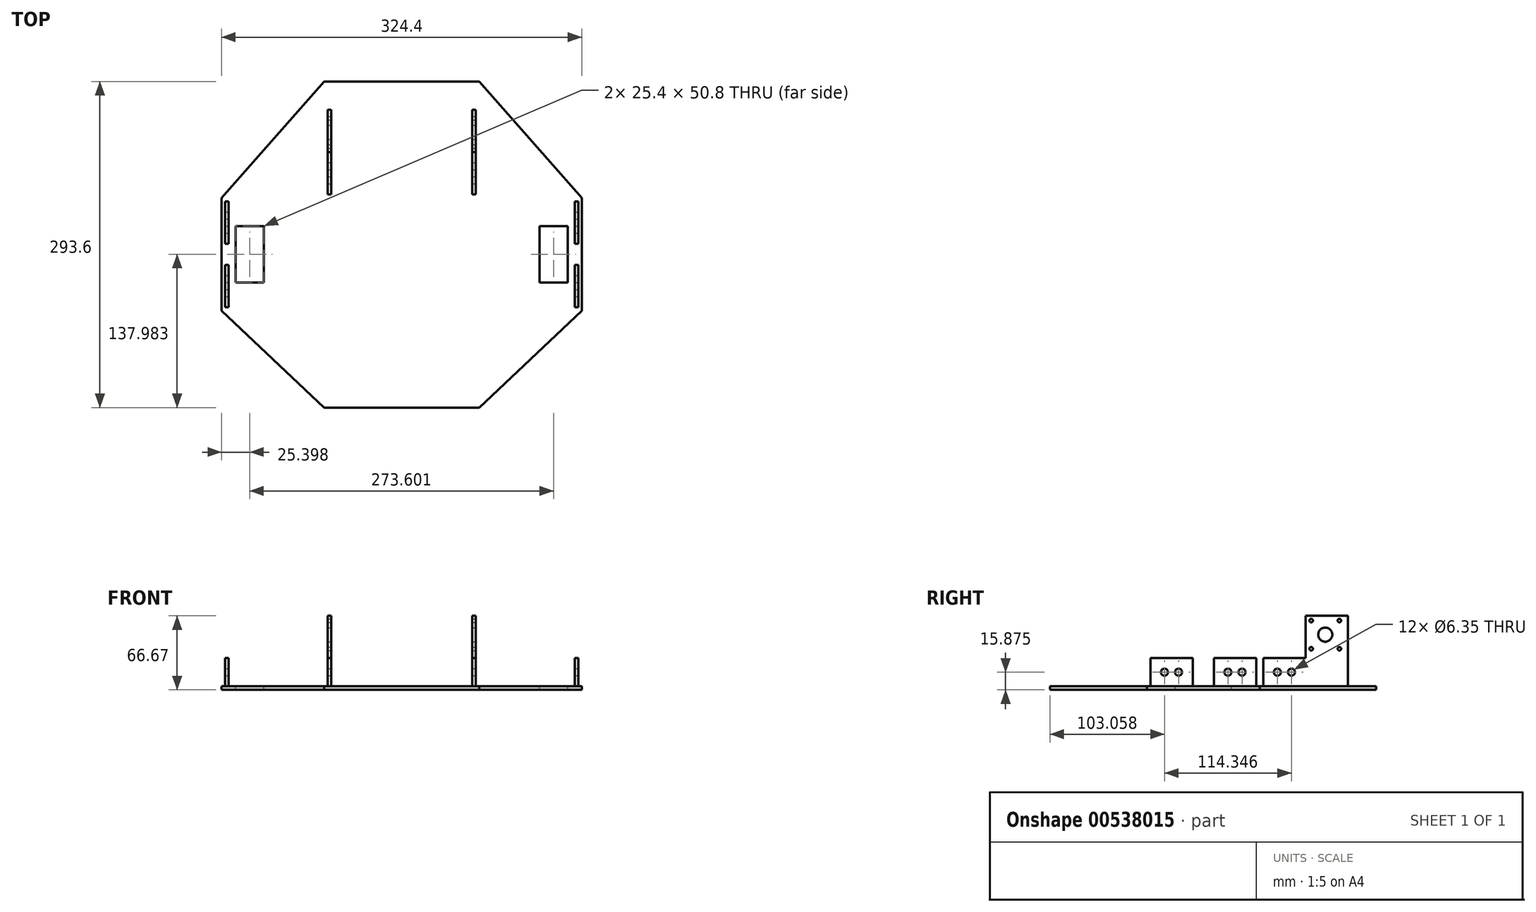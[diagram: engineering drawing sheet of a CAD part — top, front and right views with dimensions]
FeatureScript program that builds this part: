
annotation { "Feature Type Name" : "Feature", "Feature Type Description" : "" }
export const myFeature = defineFeature(function(context is Context, id is Id, definition is map)
    precondition{}
    {
        {
            var Q0;
            Q0=qCreatedBy(makeId("Top.planeOp"),FACE);
            var sketch = newSketch(context, id + "F0", { "sketchPlane" : qUnion([Q0])});
            skLineSegment(sketch, "E0", {"start": v(-252.95, -27.56) * mm, "end": v(-160.6, -114.74) * mm});
            skLineSegment(sketch, "E1", {"start": v(-160.6, -114.74) * mm, "end": v(-20.9, -114.74) * mm});
            skLineSegment(sketch, "E2", {"start": v(-20.9, -114.74) * mm, "end": v(71.45, -27.56) * mm});
            skLineSegment(sketch, "E3", {"start": v(71.45, -27.56) * mm, "end": v(71.45, 74.04) * mm});
            skLineSegment(sketch, "E4", {"start": v(71.45, 74.04) * mm, "end": v(-20.9, 178.86) * mm});
            skLineSegment(sketch, "E5", {"start": v(-20.9, 178.86) * mm, "end": v(-160.6, 178.86) * mm});
            skLineSegment(sketch, "E6", {"start": v(-160.6, 178.86) * mm, "end": v(-252.95, 74.04) * mm});
            skLineSegment(sketch, "E7", {"start": v(-252.95, 74.04) * mm, "end": v(-252.95, -27.56) * mm});
            skSolve(sketch);
        }
        {
            var Q0;
            Q0=makeQuery(id+"F0.imprint","IMPRINT",FACE,{"disambiguationData":[TD([[makeQuery(id+"F0.imprint","IMPRINT",EDGE,{"derivedFrom":sQuery(id+"F0.wireOp",EDGE,"E0")}),1.0]])]});
            extrude(context, id + "F1", {"entities" : qUnion([Q0]), "depth" : 3.17 * mm, "offsetDistance" : 25.4 * mm});
        }
        {
            var Q0;
            Q0=makeQuery(id+"F1.opExtrude","CAP_FACE",FACE,{"disambiguationData":[OSD([sQuery(id+"F0.wireOp",EDGE,"E0"),sQuery(id+"F0.wireOp",EDGE,"E1"),sQuery(id+"F0.wireOp",EDGE,"E2"),sQuery(id+"F0.wireOp",EDGE,"E3"),sQuery(id+"F0.wireOp",EDGE,"E4"),sQuery(id+"F0.wireOp",EDGE,"E5"),sQuery(id+"F0.wireOp",EDGE,"E6"),sQuery(id+"F0.wireOp",EDGE,"E7")])],"isStart":false});
            var sketch = newSketch(context, id + "F2", { "sketchPlane" : qUnion([Q0])});
            skLineSegment(sketch, "E8.bottom", {"start": v(-157.43, 115.36) * mm, "end": v(-154.25, 115.36) * mm});
            skLineSegment(sketch, "E8.top", {"start": v(-157.43, 77.26) * mm, "end": v(-154.25, 77.26) * mm});
            skLineSegment(sketch, "E8.left", {"start": v(-157.43, 115.36) * mm, "end": v(-157.43, 77.26) * mm});
            skLineSegment(sketch, "E8.right", {"start": v(-154.25, 115.36) * mm, "end": v(-154.25, 77.26) * mm});
            skLineSegment(sketch, "E9", {"start": v(-20.9, 178.86) * mm, "end": v(-20.9, -114.74) * mm});
            skLineSegment(sketch, "E10.bottom", {"start": v(-27.25, 115.36) * mm, "end": v(-24.08, 115.36) * mm});
            skLineSegment(sketch, "E10.top", {"start": v(-27.25, 77.26) * mm, "end": v(-24.08, 77.26) * mm});
            skLineSegment(sketch, "E10.left", {"start": v(-27.25, 115.36) * mm, "end": v(-27.25, 77.26) * mm});
            skLineSegment(sketch, "E10.right", {"start": v(-24.08, 115.36) * mm, "end": v(-24.08, 77.26) * mm});
            skLineSegment(sketch, "E11", {"start": v(-160.6, 178.86) * mm, "end": v(-160.6, -114.74) * mm});
            skLineSegment(sketch, "E12.bottom", {"start": v(65.1, 70.87) * mm, "end": v(68.27, 70.87) * mm});
            skLineSegment(sketch, "E12.top", {"start": v(65.1, 32.77) * mm, "end": v(68.27, 32.77) * mm});
            skLineSegment(sketch, "E12.left", {"start": v(65.1, 70.87) * mm, "end": v(65.1, 32.77) * mm});
            skLineSegment(sketch, "E12.right", {"start": v(68.27, 70.87) * mm, "end": v(68.27, 32.77) * mm});
            skLineSegment(sketch, "E13", {"start": v(-252.95, -27.56) * mm, "end": v(71.45, -27.56) * mm});
            skLineSegment(sketch, "E14", {"start": v(-252.95, 74.04) * mm, "end": v(71.45, 74.04) * mm});
            skLineSegment(sketch, "E15.bottom", {"start": v(65.1, 13.72) * mm, "end": v(68.27, 13.72) * mm});
            skLineSegment(sketch, "E15.top", {"start": v(65.1, -24.38) * mm, "end": v(68.27, -24.38) * mm});
            skLineSegment(sketch, "E15.left", {"start": v(65.1, 13.72) * mm, "end": v(65.1, -24.38) * mm});
            skLineSegment(sketch, "E15.right", {"start": v(68.27, 13.72) * mm, "end": v(68.27, -24.38) * mm});
            skLineSegment(sketch, "E16.bottom", {"start": v(-249.78, 13.72) * mm, "end": v(-246.6, 13.72) * mm});
            skLineSegment(sketch, "E16.top", {"start": v(-249.78, -24.38) * mm, "end": v(-246.6, -24.38) * mm});
            skLineSegment(sketch, "E16.left", {"start": v(-249.78, 13.72) * mm, "end": v(-249.78, -24.38) * mm});
            skLineSegment(sketch, "E16.right", {"start": v(-246.6, 13.72) * mm, "end": v(-246.6, -24.38) * mm});
            skLineSegment(sketch, "E17.bottom", {"start": v(-249.78, 70.87) * mm, "end": v(-246.6, 70.87) * mm});
            skLineSegment(sketch, "E17.top", {"start": v(-249.78, 32.77) * mm, "end": v(-246.6, 32.77) * mm});
            skLineSegment(sketch, "E17.left", {"start": v(-249.78, 70.87) * mm, "end": v(-249.78, 32.77) * mm});
            skLineSegment(sketch, "E17.right", {"start": v(-246.6, 70.87) * mm, "end": v(-246.6, 32.77) * mm});
            skLineSegment(sketch, "E18.bottom", {"start": v(-240.25, 48.64) * mm, "end": v(-214.85, 48.64) * mm});
            skLineSegment(sketch, "E18.top", {"start": v(-240.25, -2.16) * mm, "end": v(-214.85, -2.16) * mm});
            skLineSegment(sketch, "E18.left", {"start": v(-240.25, 48.64) * mm, "end": v(-240.25, -2.16) * mm});
            skLineSegment(sketch, "E18.right", {"start": v(-214.85, 48.64) * mm, "end": v(-214.85, -2.16) * mm});
            skLineSegment(sketch, "E19.bottom", {"start": v(33.35, 48.64) * mm, "end": v(58.75, 48.64) * mm});
            skLineSegment(sketch, "E19.top", {"start": v(33.35, -2.16) * mm, "end": v(58.75, -2.16) * mm});
            skLineSegment(sketch, "E19.left", {"start": v(33.35, 48.64) * mm, "end": v(33.35, -2.16) * mm});
            skLineSegment(sketch, "E19.right", {"start": v(58.75, 48.64) * mm, "end": v(58.75, -2.16) * mm});
            skLineSegment(sketch, "E20.bottom", {"start": v(-157.43, 153.46) * mm, "end": v(-154.25, 153.46) * mm});
            skLineSegment(sketch, "E20.left", {"start": v(-157.43, 153.46) * mm, "end": v(-157.43, 115.36) * mm});
            skLineSegment(sketch, "E20.right", {"start": v(-154.25, 153.46) * mm, "end": v(-154.25, 115.36) * mm});
            skLineSegment(sketch, "E21.bottom", {"start": v(-27.25, 153.46) * mm, "end": v(-24.08, 153.46) * mm});
            skLineSegment(sketch, "E21.left", {"start": v(-27.25, 153.46) * mm, "end": v(-27.25, 115.36) * mm});
            skLineSegment(sketch, "E21.right", {"start": v(-24.08, 153.46) * mm, "end": v(-24.08, 115.36) * mm});
            skSolve(sketch);
        }
        {
            var Q0;
            Q0=makeQuery(id+"F2.imprint","IMPRINT",FACE,{"disambiguationData":[TD([[makeQuery(id+"F2.imprint","IMPRINT",EDGE,{"derivedFrom":sQuery(id+"F2.wireOp",EDGE,"E17.bottom")}),-1.0]])]});
            var Q1;
            Q1=makeQuery(id+"F2.imprint","IMPRINT",FACE,{"disambiguationData":[TD([[makeQuery(id+"F2.imprint","IMPRINT",EDGE,{"derivedFrom":sQuery(id+"F2.wireOp",EDGE,"E16.bottom")}),-1.0]])]});
            var Q2;
            Q2=makeQuery(id+"F2.imprint","IMPRINT",FACE,{"disambiguationData":[TD([[makeQuery(id+"F2.imprint","IMPRINT",EDGE,{"derivedFrom":sQuery(id+"F2.wireOp",EDGE,"E8.bottom")}),-1.0]])]});
            var Q3;
            Q3=makeQuery(id+"F2.imprint","IMPRINT",FACE,{"disambiguationData":[TD([[makeQuery(id+"F2.imprint","IMPRINT",EDGE,{"derivedFrom":sQuery(id+"F2.wireOp",EDGE,"E10.bottom")}),-1.0]])]});
            var Q4;
            Q4=makeQuery(id+"F2.imprint","IMPRINT",FACE,{"disambiguationData":[TD([[makeQuery(id+"F2.imprint","IMPRINT",EDGE,{"derivedFrom":sQuery(id+"F2.wireOp",EDGE,"E12.bottom")}),-1.0]])]});
            var Q5;
            Q5=makeQuery(id+"F2.imprint","IMPRINT",FACE,{"disambiguationData":[TD([[makeQuery(id+"F2.imprint","IMPRINT",EDGE,{"derivedFrom":sQuery(id+"F2.wireOp",EDGE,"E15.bottom")}),-1.0]])]});
            extrude(context, id + "F3", {"entities" : qUnion([Q0, Q1, Q2, Q3, Q4, Q5]), "operationType" : NewBodyOperationType.ADD, "depth" : 25.4 * mm, "offsetDistance" : 25.4 * mm});
        }
        {
            var Q0;
            Q0=qCreatedBy(makeId("Right.planeOp"),FACE);
            var sketch = newSketch(context, id + "F4", { "sketchPlane" : qUnion([Q0])});
            skCircle(sketch, "E22", {"center": v(-11.68, 15.88) * mm, "radius": 3.18 * mm});
            skCircle(sketch, "E23", {"center": v(1.02, 15.88) * mm, "radius": 3.18 * mm});
            skCircle(sketch, "E24", {"center": v(45.47, 15.88) * mm, "radius": 3.18 * mm});
            skCircle(sketch, "E25", {"center": v(58.17, 15.88) * mm, "radius": 3.18 * mm});
            skCircle(sketch, "E26", {"center": v(89.96, 15.88) * mm, "radius": 3.18 * mm});
            skCircle(sketch, "E27", {"center": v(102.66, 15.88) * mm, "radius": 3.18 * mm});
            skSolve(sketch);
        }
        {
            var Q0;
            Q0=qSketchRegion(id+"F4",true);
            extrude(context, id + "F5", {"entities" : qUnion([Q0]), "operationType" : NewBodyOperationType.REMOVE, "oppositeDirection" : true, "depth" : 762 * mm, "offsetDistance" : 25.4 * mm, "symmetric" : true});
        }
        {
            var Q0;
            Q0=makeQuery(id+"F2.imprint","IMPRINT",FACE,{"disambiguationData":[TD([[makeQuery(id+"F2.imprint","IMPRINT",EDGE,{"derivedFrom":sQuery(id+"F2.wireOp",EDGE,"E18.bottom")}),-1.0]])]});
            var Q1;
            Q1=makeQuery(id+"F2.imprint","IMPRINT",FACE,{"disambiguationData":[TD([[makeQuery(id+"F2.imprint","IMPRINT",EDGE,{"derivedFrom":sQuery(id+"F2.wireOp",EDGE,"E19.bottom")}),-1.0]])]});
            extrude(context, id + "F6", {"entities" : qUnion([Q0, Q1]), "operationType" : NewBodyOperationType.REMOVE, "oppositeDirection" : true, "depth" : 25.4 * mm, "offsetDistance" : 25.4 * mm});
        }
        {
            var Q0;
            Q0=makeQuery(id+"F2.imprint","IMPRINT",FACE,{"disambiguationData":[TD([[makeQuery(id+"F2.imprint","IMPRINT",EDGE,{"derivedFrom":sQuery(id+"F2.wireOp",EDGE,"E20.bottom")}),-1.0]])]});
            var Q1;
            Q1=makeQuery(id+"F2.imprint","IMPRINT",FACE,{"disambiguationData":[TD([[makeQuery(id+"F2.imprint","IMPRINT",EDGE,{"derivedFrom":sQuery(id+"F2.wireOp",EDGE,"E21.bottom")}),-1.0]])]});
            extrude(context, id + "F7", {"entities" : qUnion([Q0, Q1]), "operationType" : NewBodyOperationType.ADD, "depth" : 63.5 * mm, "offsetDistance" : 25.4 * mm});
        }
        {
            var Q0;
            Q0=makeQuery(id+"F7.opExtrude","SWEPT_FACE",FACE,{"disambiguationData":[OSD([sQuery(id+"F2.wireOp",EDGE,"E21.right")])]});
            var sketch = newSketch(context, id + "F8", { "sketchPlane" : qUnion([Q0])});
            skCircle(sketch, "E28", {"center": v(133.13, 49.67) * mm, "radius": 6.35 * mm});
            skSolve(sketch);
        }
        {
            var Q0;
            Q0=makeQuery(id+"F8.imprint","IMPRINT",FACE,{"disambiguationData":[TD([[makeQuery(id+"F8.imprint","IMPRINT",EDGE,{"derivedFrom":sQuery(id+"F8.wireOp",EDGE,"E28")}),1.0]])]});
            var Q1;
            Q1=qSketchRegion(id+"F10",true);
            var Q2;
            Q2=makeQuery(id+"F4.imprint","IMPRINT",FACE,{"disambiguationData":[TD([[makeQuery(id+"F4.imprint","IMPRINT",EDGE,{"derivedFrom":sQuery(id+"F4.wireOp",EDGE,"E26")}),1.0]])]});
            var Q3;
            Q3=makeQuery(id+"F4.imprint","IMPRINT",FACE,{"disambiguationData":[TD([[makeQuery(id+"F4.imprint","IMPRINT",EDGE,{"derivedFrom":sQuery(id+"F4.wireOp",EDGE,"E27")}),1.0]])]});
            extrude(context, id + "F9", {"entities" : qUnion([Q0, Q1, Q2, Q3]), "operationType" : NewBodyOperationType.REMOVE, "oppositeDirection" : true, "depth" : 355.6 * mm, "offsetDistance" : 25.4 * mm, "symmetric" : true});
        }
        {
            var Q0;
            Q0=makeQuery(id+"F7.opExtrude","SWEPT_FACE",FACE,{"disambiguationData":[OSD([sQuery(id+"F2.wireOp",EDGE,"E21.right")])]});
            var sketch = newSketch(context, id + "F10", { "sketchPlane" : qUnion([Q0])});
            skLineSegment(sketch, "E29.bottom", {"start": v(145.83, 36.97) * mm, "end": v(120.43, 36.97) * mm});
            skLineSegment(sketch, "E29.top", {"start": v(145.83, 62.37) * mm, "end": v(120.43, 62.37) * mm});
            skLineSegment(sketch, "E29.left", {"start": v(145.83, 36.97) * mm, "end": v(145.83, 62.37) * mm});
            skLineSegment(sketch, "E29.right", {"start": v(120.43, 36.97) * mm, "end": v(120.43, 62.37) * mm});
            skPoint(sketch, "E29.middle", {"position": v(133.13, 49.67) * mm});
            skCircle(sketch, "E30", {"center": v(120.43, 62.37) * mm, "radius": 1.59 * mm});
            skCircle(sketch, "E31", {"center": v(145.83, 62.37) * mm, "radius": 1.59 * mm});
            skCircle(sketch, "E32", {"center": v(145.83, 36.97) * mm, "radius": 1.59 * mm});
            skCircle(sketch, "E33", {"center": v(120.43, 36.97) * mm, "radius": 1.59 * mm});
            skSolve(sketch);
        }
        {
            var Q0;
            {var subQ0=sQuery(id+"F10.wireOp",EDGE,"E29.right");var subQ1=sQuery(id+"F10.wireOp",EDGE,"E29.top");var subQ2=makeQuery(id+"F10.imprint","INTERSECT",VERTEX,{"derivedFrom":[subQ1,subQ0]});Q0=makeQuery(id+"F10.imprint","IMPRINT",FACE,{"disambiguationData":[TD([[makeQuery(id+"F10.imprint","IMPRINT",EDGE,{"disambiguationData":[TD([[subQ2,1.0]])],"derivedFrom":subQ1}),-1.0]])]});}
            var Q1;
            {var subQ0=sQuery(id+"F10.wireOp",EDGE,"E29.left");var subQ1=sQuery(id+"F10.wireOp",EDGE,"E29.top");var subQ2=makeQuery(id+"F10.imprint","INTERSECT",VERTEX,{"derivedFrom":[subQ1,subQ0]});Q1=makeQuery(id+"F10.imprint","IMPRINT",FACE,{"disambiguationData":[TD([[makeQuery(id+"F10.imprint","IMPRINT",EDGE,{"disambiguationData":[TD([[subQ2,-1.0]])],"derivedFrom":subQ1}),-1.0]])]});}
            var Q2;
            {var subQ0=sQuery(id+"F10.wireOp",EDGE,"E29.left");var subQ1=sQuery(id+"F10.wireOp",EDGE,"E29.bottom");var subQ2=makeQuery(id+"F10.imprint","INTERSECT",VERTEX,{"derivedFrom":[subQ1,subQ0]});Q2=makeQuery(id+"F10.imprint","IMPRINT",FACE,{"disambiguationData":[TD([[makeQuery(id+"F10.imprint","IMPRINT",EDGE,{"disambiguationData":[TD([[subQ2,-1.0]])],"derivedFrom":subQ1}),1.0]])]});}
            var Q3;
            {var subQ0=sQuery(id+"F10.wireOp",EDGE,"E29.right");var subQ1=sQuery(id+"F10.wireOp",EDGE,"E29.bottom");var subQ2=makeQuery(id+"F10.imprint","INTERSECT",VERTEX,{"derivedFrom":[subQ1,subQ0]});Q3=makeQuery(id+"F10.imprint","IMPRINT",FACE,{"disambiguationData":[TD([[makeQuery(id+"F10.imprint","IMPRINT",EDGE,{"disambiguationData":[TD([[subQ2,1.0]])],"derivedFrom":subQ1}),1.0]])]});}
            var Q4;
            {var subQ0=sQuery(id+"F10.wireOp",EDGE,"E29.right");var subQ1=sQuery(id+"F10.wireOp",EDGE,"E29.bottom");var subQ2=makeQuery(id+"F10.imprint","INTERSECT",VERTEX,{"derivedFrom":[subQ1,subQ0]});Q4=makeQuery(id+"F10.imprint","IMPRINT",FACE,{"disambiguationData":[TD([[makeQuery(id+"F10.imprint","IMPRINT",EDGE,{"disambiguationData":[TD([[subQ2,1.0]])],"derivedFrom":subQ1}),-1.0]])]});}
            var Q5;
            {var subQ0=sQuery(id+"F10.wireOp",EDGE,"E29.right");var subQ1=sQuery(id+"F10.wireOp",EDGE,"E29.top");var subQ2=makeQuery(id+"F10.imprint","INTERSECT",VERTEX,{"derivedFrom":[subQ1,subQ0]});Q5=makeQuery(id+"F10.imprint","IMPRINT",FACE,{"disambiguationData":[TD([[makeQuery(id+"F10.imprint","IMPRINT",EDGE,{"disambiguationData":[TD([[subQ2,1.0]])],"derivedFrom":subQ1}),1.0]])]});}
            var Q6;
            {var subQ0=sQuery(id+"F10.wireOp",EDGE,"E29.left");var subQ1=sQuery(id+"F10.wireOp",EDGE,"E29.top");var subQ2=makeQuery(id+"F10.imprint","INTERSECT",VERTEX,{"derivedFrom":[subQ1,subQ0]});Q6=makeQuery(id+"F10.imprint","IMPRINT",FACE,{"disambiguationData":[TD([[makeQuery(id+"F10.imprint","IMPRINT",EDGE,{"disambiguationData":[TD([[subQ2,-1.0]])],"derivedFrom":subQ1}),1.0]])]});}
            var Q7;
            {var subQ0=sQuery(id+"F10.wireOp",EDGE,"E29.left");var subQ1=sQuery(id+"F10.wireOp",EDGE,"E29.bottom");var subQ2=makeQuery(id+"F10.imprint","INTERSECT",VERTEX,{"derivedFrom":[subQ1,subQ0]});Q7=makeQuery(id+"F10.imprint","IMPRINT",FACE,{"disambiguationData":[TD([[makeQuery(id+"F10.imprint","IMPRINT",EDGE,{"disambiguationData":[TD([[subQ2,-1.0]])],"derivedFrom":subQ1}),-1.0]])]});}
            extrude(context, id + "F11", {"entities" : qUnion([Q0, Q1, Q2, Q3, Q4, Q5, Q6, Q7]), "operationType" : NewBodyOperationType.REMOVE, "oppositeDirection" : true, "depth" : 304.8 * mm, "offsetDistance" : 25.4 * mm});
        }
        {
            var Q0;
            Q0=makeQuery(id+"F2.imprint","IMPRINT",FACE,{"disambiguationData":[TD([[makeQuery(id+"F2.imprint","IMPRINT",EDGE,{"derivedFrom":sQuery(id+"F2.wireOp",EDGE,"E10.top")}),1.0]])]});
            var Q1;
            Q1=makeQuery(id+"F2.imprint","IMPRINT",FACE,{"disambiguationData":[TD([[makeQuery(id+"F2.imprint","IMPRINT",EDGE,{"derivedFrom":sQuery(id+"F2.wireOp",EDGE,"E8.top")}),1.0]])]});
            extrude(context, id + "F12", {"entities" : qUnion([Q0, Q1]), "operationType" : NewBodyOperationType.ADD, "depth" : 25.4 * mm, "offsetDistance" : 25.4 * mm});
        }
        {
            var Q0;
            Q0=makeQuery(id+"F4.imprint","IMPRINT",FACE,{"disambiguationData":[TD([[makeQuery(id+"F4.imprint","IMPRINT",EDGE,{"derivedFrom":sQuery(id+"F4.wireOp",EDGE,"E27")}),1.0]])]});
            var Q1;
            Q1=makeQuery(id+"F4.imprint","IMPRINT",FACE,{"disambiguationData":[TD([[makeQuery(id+"F4.imprint","IMPRINT",EDGE,{"derivedFrom":sQuery(id+"F4.wireOp",EDGE,"E26")}),1.0]])]});
            extrude(context, id + "F13", {"entities" : qUnion([Q0, Q1]), "operationType" : NewBodyOperationType.REMOVE, "oppositeDirection" : true, "depth" : 254 * mm, "offsetDistance" : 25.4 * mm});
        }
    });
